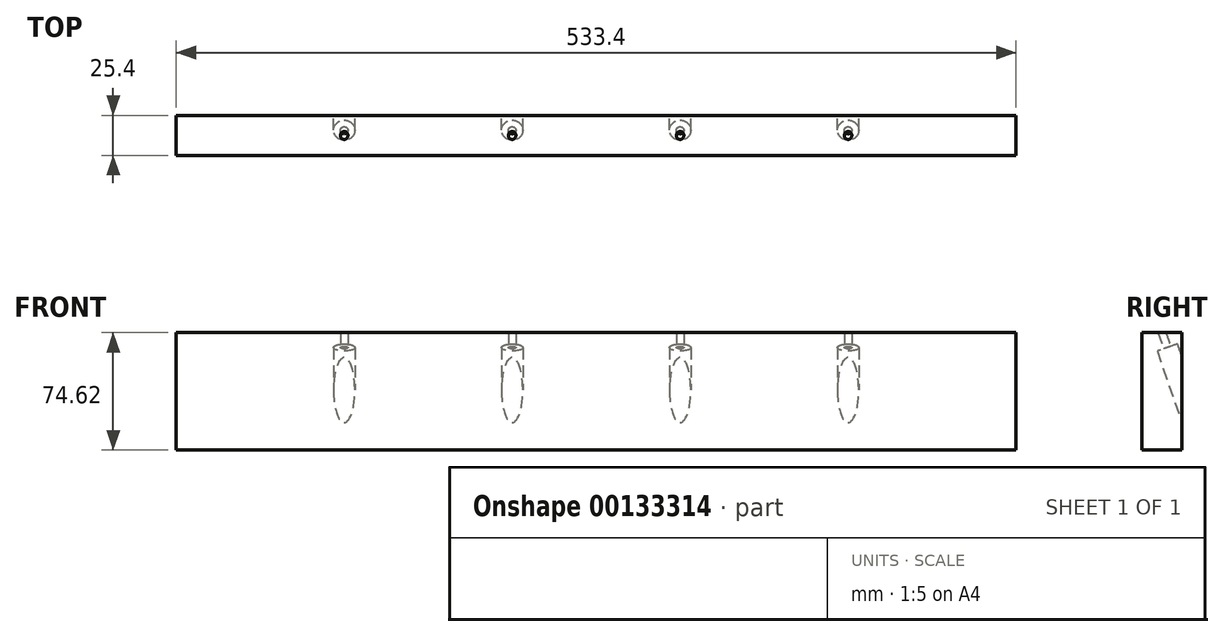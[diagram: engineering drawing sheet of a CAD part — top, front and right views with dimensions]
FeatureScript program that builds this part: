
annotation { "Feature Type Name" : "Feature", "Feature Type Description" : "" }
export const myFeature = defineFeature(function(context is Context, id is Id, definition is map)
    precondition{}
    {
        {
            var Q0;
            Q0=qCreatedBy(makeId("Front.planeOp"),FACE);
            var sketch = newSketch(context, id + "F0", { "sketchPlane" : qUnion([Q0])});
            skLineSegment(sketch, "E0.bottom", {"start": v(266.7, -37.3) * mm, "end": v(-266.7, -37.3) * mm});
            skLineSegment(sketch, "E0.top", {"start": v(266.7, 37.3) * mm, "end": v(-266.7, 37.3) * mm});
            skLineSegment(sketch, "E0.left", {"start": v(266.7, -37.3) * mm, "end": v(266.7, 37.3) * mm});
            skLineSegment(sketch, "E0.right", {"start": v(-266.7, -37.3) * mm, "end": v(-266.7, 37.3) * mm});
            skPoint(sketch, "E0.middle", {"position": v(0, 0) * mm});
            skSolve(sketch);
        }
        {
            var Q0;
            Q0=makeQuery(id+"F0.imprint","IMPRINT",FACE,{"disambiguationData":[TD([[makeQuery(id+"F0.imprint","IMPRINT",EDGE,{"derivedFrom":sQuery(id+"F0.wireOp",EDGE,"E0.bottom")}),-1.0]])]});
            extrude(context, id + "F1", {"entities" : qUnion([Q0]), "depth" : 25.4 * mm});
        }
        {
            var Q0;
            Q0=qCreatedBy(makeId("Right.planeOp"),FACE);
            var sketch = newSketch(context, id + "F2", { "sketchPlane" : qUnion([Q0])});
            skLineSegment(sketch, "E1", {"start": v(-29.87, -12.8) * mm, "end": v(-19.57, -9.22) * mm});
            skLineSegment(sketch, "E2", {"start": v(38.16, 13.38) * mm, "end": v(-38.16, -13.17) * mm});
            skLineSegment(sketch, "E3", {"start": v(-19.57, -9.22) * mm, "end": v(-18.12, -13.38) * mm});
            skLineSegment(sketch, "E4", {"start": v(27.28, 2.41) * mm, "end": v(-18.12, -13.38) * mm});
            skLineSegment(sketch, "E5", {"start": v(25.05, 8.82) * mm, "end": v(27.28, 2.41) * mm});
            skLineSegment(sketch, "E6", {"start": v(-29.87, -12.8) * mm, "end": v(-30.66, -10.56) * mm});
            skLineSegment(sketch, "E7", {"start": v(-29.87, -10.29) * mm, "end": v(-29.87, 2.41) * mm});
            skLineSegment(sketch, "E8", {"start": v(-29.87, 2.41) * mm, "end": v(6.64, 2.41) * mm});
            skSolve(sketch);
        }
        {
            var Q0;
            Q0=makeQuery(id+"F2.imprint","IMPRINT",FACE,{"disambiguationData":[TD([[makeQuery(id+"F2.imprint","IMPRINT",EDGE,{"derivedFrom":sQuery(id+"F2.wireOp",EDGE,"E1")}),1.0]])]});
            var Q1;
            Q1=sQuery(id+"F2.wireOp",EDGE,"E2");
            revolve(context, id + "F3", {"entities" : qUnion([Q0]), "axis" : qUnion([Q1]), "revolveType" : RevolveType.FULL});
        }
        {
            var Q0;
            Q0=makeQuery(id+"F1.opExtrude","SWEPT_FACE",FACE,{"disambiguationData":[OSD([sQuery(id+"F0.wireOp",EDGE,"E0.top")])]});
            var sketch = newSketch(context, id + "F4", { "sketchPlane" : qUnion([Q0])});
            skLineSegment(sketch, "E9.0", {"start": v(266.7, 0) * mm, "end": v(-266.7, 0) * mm});
            skPoint(sketch, "E10", {"position": v(-160.02, 0) * mm});
            skPoint(sketch, "E11", {"position": v(-53.34, 0) * mm});
            skPoint(sketch, "E12", {"position": v(53.34, 0) * mm});
            skPoint(sketch, "E13", {"position": v(160.02, 0) * mm});
            skSolve(sketch);
        }
        {
            var Q0;
            Q0=makeQuery(id+"F3.opRevolve","SWEPT_BODY",BODY,{"disambiguationData":[OSD([sQuery(id+"F2.wireOp",EDGE,"E1"),sQuery(id+"F2.wireOp",EDGE,"E2"),sQuery(id+"F2.wireOp",EDGE,"E3"),sQuery(id+"F2.wireOp",EDGE,"E4"),sQuery(id+"F2.wireOp",EDGE,"E5"),sQuery(id+"F2.wireOp",EDGE,"E6")])]});
            var Q1;
            Q1=sQuery(id+"F2.wireOp",VERTEX,"E8.start");
            var Q2;
            Q2=sQuery(id+"F4.wireOp",VERTEX,"E10");
            transform(context, id + "F5", {"entities" : qUnion([Q0]), "transformType" : TransformType.TRANSLATION_ENTITY, "oppositeDirectionEntity" : false, "transformLine" : qUnion([Q1, Q2]), "makeCopy" : true});
        }
        {
            var Q0;
            Q0=makeQuery(id+"F5.opPattern","COPY",BODY,{"derivedFrom":makeQuery(id+"F3.opRevolve","SWEPT_BODY",BODY,{"disambiguationData":[OSD([sQuery(id+"F2.wireOp",EDGE,"E1"),sQuery(id+"F2.wireOp",EDGE,"E2"),sQuery(id+"F2.wireOp",EDGE,"E3"),sQuery(id+"F2.wireOp",EDGE,"E4"),sQuery(id+"F2.wireOp",EDGE,"E5"),sQuery(id+"F2.wireOp",EDGE,"E6")])]}),"instanceName":"1"});
            var Q1;
            Q1=makeQuery(id+"F1.opExtrude","CAP_EDGE",EDGE,{"disambiguationData":[OSD([sQuery(id+"F0.wireOp",EDGE,"E0.top")])],"isStart":true});
            transform(context, id + "F6", {"entities" : qUnion([Q0]), "transformType" : TransformType.ROTATION, "transformAxis" : qUnion([Q1]), "angle" : 90 * degree, "makeCopy" : false});
        }
        {
            var Q0;
            Q0=makeQuery(id+"F3.opRevolve","SWEPT_BODY",BODY,{"disambiguationData":[OSD([sQuery(id+"F2.wireOp",EDGE,"E1"),sQuery(id+"F2.wireOp",EDGE,"E2"),sQuery(id+"F2.wireOp",EDGE,"E3"),sQuery(id+"F2.wireOp",EDGE,"E4"),sQuery(id+"F2.wireOp",EDGE,"E5"),sQuery(id+"F2.wireOp",EDGE,"E6")])]});
            var Q1;
            Q1=sQuery(id+"F2.wireOp",VERTEX,"E8.start");
            var Q2;
            Q2=sQuery(id+"F4.wireOp",VERTEX,"E11");
            transform(context, id + "F7", {"entities" : qUnion([Q0]), "transformType" : TransformType.TRANSLATION_ENTITY, "oppositeDirectionEntity" : false, "transformLine" : qUnion([Q1, Q2]), "makeCopy" : true});
        }
        {
            var Q0;
            Q0=makeQuery(id+"F3.opRevolve","SWEPT_BODY",BODY,{"disambiguationData":[OSD([sQuery(id+"F2.wireOp",EDGE,"E1"),sQuery(id+"F2.wireOp",EDGE,"E2"),sQuery(id+"F2.wireOp",EDGE,"E3"),sQuery(id+"F2.wireOp",EDGE,"E4"),sQuery(id+"F2.wireOp",EDGE,"E5"),sQuery(id+"F2.wireOp",EDGE,"E6")])]});
            var Q1;
            Q1=sQuery(id+"F2.wireOp",VERTEX,"E8.start");
            var Q2;
            Q2=sQuery(id+"F4.wireOp",VERTEX,"E12");
            transform(context, id + "F8", {"entities" : qUnion([Q0]), "transformType" : TransformType.TRANSLATION_ENTITY, "oppositeDirectionEntity" : false, "transformLine" : qUnion([Q1, Q2]), "makeCopy" : true});
        }
        {
            var Q0;
            Q0=makeQuery(id+"F3.opRevolve","SWEPT_BODY",BODY,{"disambiguationData":[OSD([sQuery(id+"F2.wireOp",EDGE,"E1"),sQuery(id+"F2.wireOp",EDGE,"E2"),sQuery(id+"F2.wireOp",EDGE,"E3"),sQuery(id+"F2.wireOp",EDGE,"E4"),sQuery(id+"F2.wireOp",EDGE,"E5"),sQuery(id+"F2.wireOp",EDGE,"E6")])]});
            var Q1;
            Q1=sQuery(id+"F2.wireOp",VERTEX,"E8.start");
            var Q2;
            Q2=sQuery(id+"F4.wireOp",VERTEX,"E13");
            transform(context, id + "F9", {"entities" : qUnion([Q0]), "transformType" : TransformType.TRANSLATION_ENTITY, "oppositeDirectionEntity" : false, "transformLine" : qUnion([Q1, Q2]), "makeCopy" : false});
        }
        {
            var Q0;
            Q0=makeQuery(id+"F7.opPattern","COPY",BODY,{"derivedFrom":makeQuery(id+"F3.opRevolve","SWEPT_BODY",BODY,{"disambiguationData":[OSD([sQuery(id+"F2.wireOp",EDGE,"E1"),sQuery(id+"F2.wireOp",EDGE,"E2"),sQuery(id+"F2.wireOp",EDGE,"E3"),sQuery(id+"F2.wireOp",EDGE,"E4"),sQuery(id+"F2.wireOp",EDGE,"E5"),sQuery(id+"F2.wireOp",EDGE,"E6")])]}),"instanceName":"1"});
            var Q1;
            Q1=makeQuery(id+"F8.opPattern","COPY",BODY,{"derivedFrom":makeQuery(id+"F3.opRevolve","SWEPT_BODY",BODY,{"disambiguationData":[OSD([sQuery(id+"F2.wireOp",EDGE,"E1"),sQuery(id+"F2.wireOp",EDGE,"E2"),sQuery(id+"F2.wireOp",EDGE,"E3"),sQuery(id+"F2.wireOp",EDGE,"E4"),sQuery(id+"F2.wireOp",EDGE,"E5"),sQuery(id+"F2.wireOp",EDGE,"E6")])]}),"instanceName":"1"});
            var Q2;
            Q2=makeQuery(id+"F3.opRevolve","SWEPT_BODY",BODY,{"disambiguationData":[OSD([sQuery(id+"F2.wireOp",EDGE,"E1"),sQuery(id+"F2.wireOp",EDGE,"E2"),sQuery(id+"F2.wireOp",EDGE,"E3"),sQuery(id+"F2.wireOp",EDGE,"E4"),sQuery(id+"F2.wireOp",EDGE,"E5"),sQuery(id+"F2.wireOp",EDGE,"E6")])]});
            var Q3;
            Q3=sQuery(id+"F4.wireOp",EDGE,"E9.0");
            transform(context, id + "F10", {"entities" : qUnion([Q0, Q1, Q2]), "transformType" : TransformType.ROTATION, "transformAxis" : qUnion([Q3]), "angle" : 90 * degree, "makeCopy" : false});
        }
        {
            var Q0;
            Q0=makeQuery(id+"F3.opRevolve","SWEPT_BODY",BODY,{"disambiguationData":[OSD([sQuery(id+"F2.wireOp",EDGE,"E1"),sQuery(id+"F2.wireOp",EDGE,"E2"),sQuery(id+"F2.wireOp",EDGE,"E3"),sQuery(id+"F2.wireOp",EDGE,"E4"),sQuery(id+"F2.wireOp",EDGE,"E5"),sQuery(id+"F2.wireOp",EDGE,"E6")])]});
            var Q1;
            Q1=makeQuery(id+"F8.opPattern","COPY",BODY,{"derivedFrom":makeQuery(id+"F3.opRevolve","SWEPT_BODY",BODY,{"disambiguationData":[OSD([sQuery(id+"F2.wireOp",EDGE,"E1"),sQuery(id+"F2.wireOp",EDGE,"E2"),sQuery(id+"F2.wireOp",EDGE,"E3"),sQuery(id+"F2.wireOp",EDGE,"E4"),sQuery(id+"F2.wireOp",EDGE,"E5"),sQuery(id+"F2.wireOp",EDGE,"E6")])]}),"instanceName":"1"});
            var Q2;
            Q2=makeQuery(id+"F7.opPattern","COPY",BODY,{"derivedFrom":makeQuery(id+"F3.opRevolve","SWEPT_BODY",BODY,{"disambiguationData":[OSD([sQuery(id+"F2.wireOp",EDGE,"E1"),sQuery(id+"F2.wireOp",EDGE,"E2"),sQuery(id+"F2.wireOp",EDGE,"E3"),sQuery(id+"F2.wireOp",EDGE,"E4"),sQuery(id+"F2.wireOp",EDGE,"E5"),sQuery(id+"F2.wireOp",EDGE,"E6")])]}),"instanceName":"1"});
            var Q3;
            Q3=makeQuery(id+"F5.opPattern","COPY",BODY,{"derivedFrom":makeQuery(id+"F3.opRevolve","SWEPT_BODY",BODY,{"disambiguationData":[OSD([sQuery(id+"F2.wireOp",EDGE,"E1"),sQuery(id+"F2.wireOp",EDGE,"E2"),sQuery(id+"F2.wireOp",EDGE,"E3"),sQuery(id+"F2.wireOp",EDGE,"E4"),sQuery(id+"F2.wireOp",EDGE,"E5"),sQuery(id+"F2.wireOp",EDGE,"E6")])]}),"instanceName":"1"});
            var Q4;
            Q4=makeQuery(id+"F1.opExtrude","SWEPT_BODY",BODY,{"disambiguationData":[OSD([sQuery(id+"F0.wireOp",EDGE,"E0.bottom"),sQuery(id+"F0.wireOp",EDGE,"E0.top"),sQuery(id+"F0.wireOp",EDGE,"E0.left"),sQuery(id+"F0.wireOp",EDGE,"E0.right")])]});
            booleanBodies(context, id + "F11", {"operationType" : BooleanOperationType.SUBTRACTION, "tools" : qUnion([Q0, Q1, Q2, Q3]), "targets" : qUnion([Q4])});
        }
    });
